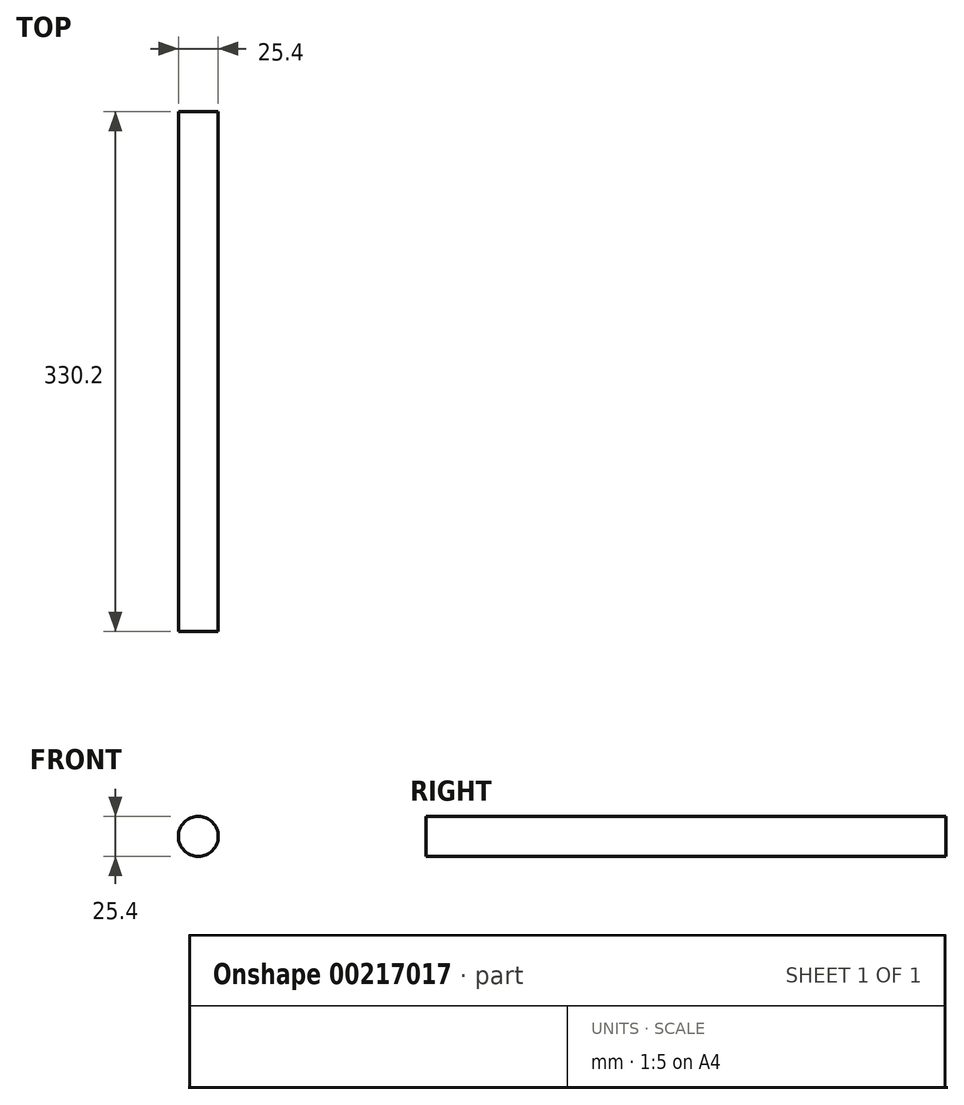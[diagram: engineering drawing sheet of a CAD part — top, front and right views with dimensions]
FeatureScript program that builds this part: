
annotation { "Feature Type Name" : "Feature", "Feature Type Description" : "" }
export const myFeature = defineFeature(function(context is Context, id is Id, definition is map)
    precondition{}
    {
        {
            var Q0;
            Q0=qCreatedBy(makeId("Front.planeOp"),FACE);
            var sketch = newSketch(context, id + "F0", { "sketchPlane" : qUnion([Q0])});
            skCircle(sketch, "E0", {"center": v(0, -3.24) * mm, "radius": 12.7 * mm});
            skCircle(sketch, "E1", {"center": v(0, -3.24) * mm, "radius": 15.88 * mm});
            skSolve(sketch);
        }
        {
            var Q0;
            Q0=makeQuery(id+"F0.imprint","IMPRINT",FACE,{"disambiguationData":[TD([[makeQuery(id+"F0.imprint","IMPRINT",EDGE,{"derivedFrom":sQuery(id+"F0.wireOp",EDGE,"E0")}),1.0]])]});
            extrude(context, id + "F1", {"entities" : qUnion([Q0]), "depth" : 508 * mm});
        }
        {
            var Q0;
            Q0=makeQuery(id+"F1.opExtrude","CAP_FACE",FACE,{"disambiguationData":[OSD([sQuery(id+"F0.wireOp",EDGE,"E0")])],"isStart":false});
            extrude(context, id + "F2", {"entities" : qUnion([Q0]), "operationType" : NewBodyOperationType.REMOVE, "oppositeDirection" : true, "depth" : 127 * mm});
        }
        {
            var Q0;
            Q0=makeQuery(id+"F2.boolean.opBoolean","COPY",FACE,{"derivedFrom":makeQuery(id+"F2.opExtrude","CAP_FACE",FACE,{"disambiguationData":[OSD([sQuery(id+"F0.wireOp",EDGE,"E0")])],"isStart":false})});
            extrude(context, id + "F3", {"entities" : qUnion([Q0]), "operationType" : NewBodyOperationType.REMOVE, "oppositeDirection" : true, "depth" : 50.8 * mm});
        }
    });
